# Revit family: PRD_FrankeWS_Shlvs_STRATOSShelf_STRX624
name_source: partatom
category: Specialty Equipment
revit_build: Autodesk Revit 2018 (Build: 20190510_1515(x64)
units: mm (PartAtom-declared; Revit-internal decimal feet)

## family parameters
Cut with Voids When Loaded = No
Host = Face
OmniClass Number = 23.40.20.21
OmniClass Title = Toilet and Bath Specialties
Part Type = Normal
Room Calculation Point = No
Round Connector Dimension = Use Diameter
Shared = No

## types (1)
- STRX624
    AssetType = Fixed
    BIMObjectName = PRD_AR_Shelves_STRATOSShelf_STRX624
    Category = Pr_40_30_78_06, Bathroom shelves
    Default Elevation = 1600 mm  [stored 5.24934 ft]
    Description = Shelf for wall mounting, stainless steel, surface satin finished, front with InoxPlus surface refinement for the reduction of finger marks and better cleaning characteristics (easy to clean), material thickness 2 mm, rounded edges, protection edge at front, includes stainless steel screws and dowels.
    DurationUnit = year
    Features = stainless steel, surface satin finished
    Finish = satin finished
    GrossWeight = 1.71 kg
    IfcExportAs = IfcFurnitureType
    IfcExportType = USERDEFINED
    IsBuiltIn = TRUE
    MainColor = stainless steel
    Manufacturer = KWC Group AG
    ManufacturerName = KWC Group AG
    ManufacturerURL = www.kwc.com
    Material = stainless steel
    MaterialCode = 1.4301
    MaterialThickness = 2.00 mm
    Model = STRX624
    ModelNumber = 2000102701
    ModelReference = STRX624
    NBSDescription = Shelves
    NBSReference = 45-35-72/354
    Name = STRATOS shelf STRX624
    NetWeight = 1.54 kg
    NominalDepth = 110 mm  [stored 0.360892 ft]
    NominalHeight = 45 mm  [stored 0.147638 ft]
    NominalWidth = 600 mm
    ProductInformation = https://pim.kwc.com
    ShelfMaterial = PRD_AR_StainlessSteel_SatinFinished
    Size = 600 x 45 x 110 mm
    SurfaceTreatment = InoxPlus (anti fingerprint)
    TypeOfFixing = Screw
    TypeOfMounting = Wall mounting
    URL = www.kwc.com
    Uniclass2015Code = Pr_40_30_78_06
    Uniclass2015Title = Bathroom shelves
    Uniclass2015Version = Products v1.10
    Version = 1
    WarrantyDurationUnit = year

note: [stored X ft] marks values corroborated as IEEE doubles in the binary element streams (Revit-internal decimal feet)

## geometry (parser evidence)
native form markers: Sweep x2
no freeform markers — native parametric forms only
